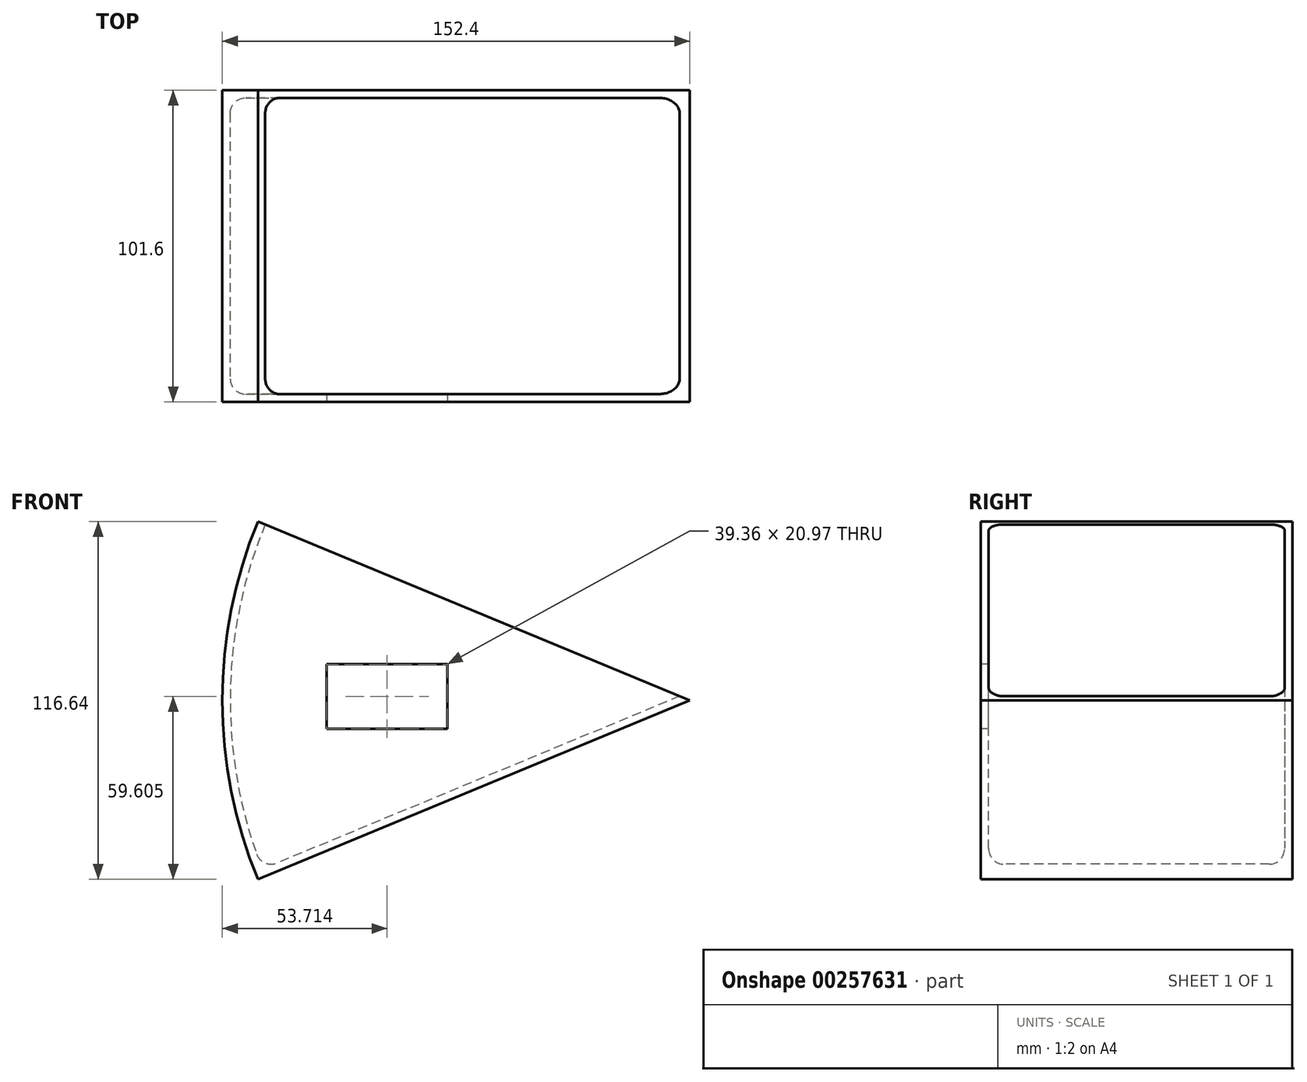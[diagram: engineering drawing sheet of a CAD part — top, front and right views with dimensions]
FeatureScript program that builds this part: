
annotation { "Feature Type Name" : "Feature", "Feature Type Description" : "" }
export const myFeature = defineFeature(function(context is Context, id is Id, definition is map)
    precondition{}
    {
        {
            var Q0;
            Q0=qCreatedBy(makeId("Top.planeOp"),FACE);
            var sketch = newSketch(context, id + "F0", { "sketchPlane" : qUnion([Q0])});
            skLineSegment(sketch, "E0", {"start": v(0, 0) * mm, "end": v(-152.4, 0) * mm});
            skLineSegment(sketch, "E1", {"start": v(-152.4, 0) * mm, "end": v(-152.4, -101.6) * mm});
            skLineSegment(sketch, "E2", {"start": v(-152.4, -101.6) * mm, "end": v(0, -101.6) * mm});
            skLineSegment(sketch, "E3", {"start": v(0, -101.6) * mm, "end": v(0, 0) * mm});
            skSolve(sketch);
        }
        {
            var Q0;
            Q0=makeQuery(id+"F0.imprint","IMPRINT",FACE,{"disambiguationData":[TD([[makeQuery(id+"F0.imprint","IMPRINT",EDGE,{"derivedFrom":sQuery(id+"F0.wireOp",EDGE,"E0")}),1.0]])]});
            var Q1;
            Q1=sQuery(id+"F0.wireOp",EDGE,"E3");
            revolve(context, id + "F1", {"entities" : qUnion([Q0]), "axis" : qUnion([Q1]), "revolveType" : RevolveType.SYMMETRIC, "angle" : 45 * degree});
        }
        {
            var Q0;
            Q0=makeQuery(id+"F1.opRevolve","CAP_FACE",FACE,{"disambiguationData":[OSD([sQuery(id+"F0.wireOp",EDGE,"E0"),sQuery(id+"F0.wireOp",EDGE,"E1"),sQuery(id+"F0.wireOp",EDGE,"E2"),sQuery(id+"F0.wireOp",EDGE,"E3")])],"isStart":false});
            shell(context, id + "F2", {"entities" : qUnion([Q0]), "thickness" : 2.54 * mm});
        }
        {
            var Q0;
            {var subQ0=sQuery(id+"F0.wireOp",EDGE,"E2");Q0=makeQuery(id+"F2.opShell","OFFSET_EDGE",EDGE,{"disambiguationData":[OSD([subQ0]),TDD([makeQuery(id+"F1.opRevolve","CAP_EDGE",EDGE,{"disambiguationData":[OSD([subQ0])],"isStart":true})])]});}
            var Q1;
            Q1=makeQuery(id+"F2.opShell","OFFSET_EDGE",EDGE,{"disambiguationData":[OSD([sQuery(id+"F0.wireOp",EDGE,"E1"),sQuery(id+"F0.wireOp",EDGE,"E2")])]});
            var Q2;
            {var subQ0=sQuery(id+"F0.wireOp",EDGE,"E1");Q2=makeQuery(id+"F2.opShell","OFFSET_EDGE",EDGE,{"disambiguationData":[OSD([subQ0]),TDD([makeQuery(id+"F1.opRevolve","CAP_EDGE",EDGE,{"disambiguationData":[OSD([subQ0])],"isStart":true})])]});}
            var Q3;
            {var subQ0=sQuery(id+"F0.wireOp",EDGE,"E0");Q3=makeQuery(id+"F2.opShell","OFFSET_EDGE",EDGE,{"disambiguationData":[OSD([subQ0]),TDD([makeQuery(id+"F1.opRevolve","CAP_EDGE",EDGE,{"disambiguationData":[OSD([subQ0])],"isStart":true})])]});}
            var Q4;
            Q4=makeQuery(id+"F2.opShell","OFFSET_EDGE",EDGE,{"disambiguationData":[OSD([sQuery(id+"F0.wireOp",EDGE,"E0"),sQuery(id+"F0.wireOp",EDGE,"E1")])]});
            fillet(context, id + "F3", {"entities" : qUnion([Q0, Q1, Q2, Q3, Q4]), "radius" : 5.08 * mm, "tangentPropagation" : true, "allowEdgeOverflow" : false});
        }
        {
            var Q0;
            Q0=makeQuery(id+"F1.opRevolve","SWEPT_FACE",FACE,{"disambiguationData":[OSD([sQuery(id+"F0.wireOp",EDGE,"E2")])]});
            var sketch = newSketch(context, id + "F4", { "sketchPlane" : qUnion([Q0])});
            skLineSegment(sketch, "E4.bottom", {"start": v(-118.37, 11.77) * mm, "end": v(-79, 11.77) * mm});
            skLineSegment(sketch, "E4.top", {"start": v(-118.37, -9.2) * mm, "end": v(-79, -9.2) * mm});
            skLineSegment(sketch, "E4.left", {"start": v(-118.37, 11.77) * mm, "end": v(-118.37, -9.2) * mm});
            skLineSegment(sketch, "E4.right", {"start": v(-79, 11.77) * mm, "end": v(-79, -9.2) * mm});
            skSolve(sketch);
        }
        {
            var Q0;
            Q0=makeQuery(id+"F4.imprint","IMPRINT",FACE,{"disambiguationData":[TD([[makeQuery(id+"F4.imprint","IMPRINT",EDGE,{"derivedFrom":sQuery(id+"F4.wireOp",EDGE,"E4.bottom")}),-1.0]])]});
            extrude(context, id + "F5", {"entities" : qUnion([Q0]), "operationType" : NewBodyOperationType.REMOVE, "oppositeDirection" : true, "depth" : 25.4 * mm});
        }
    });
